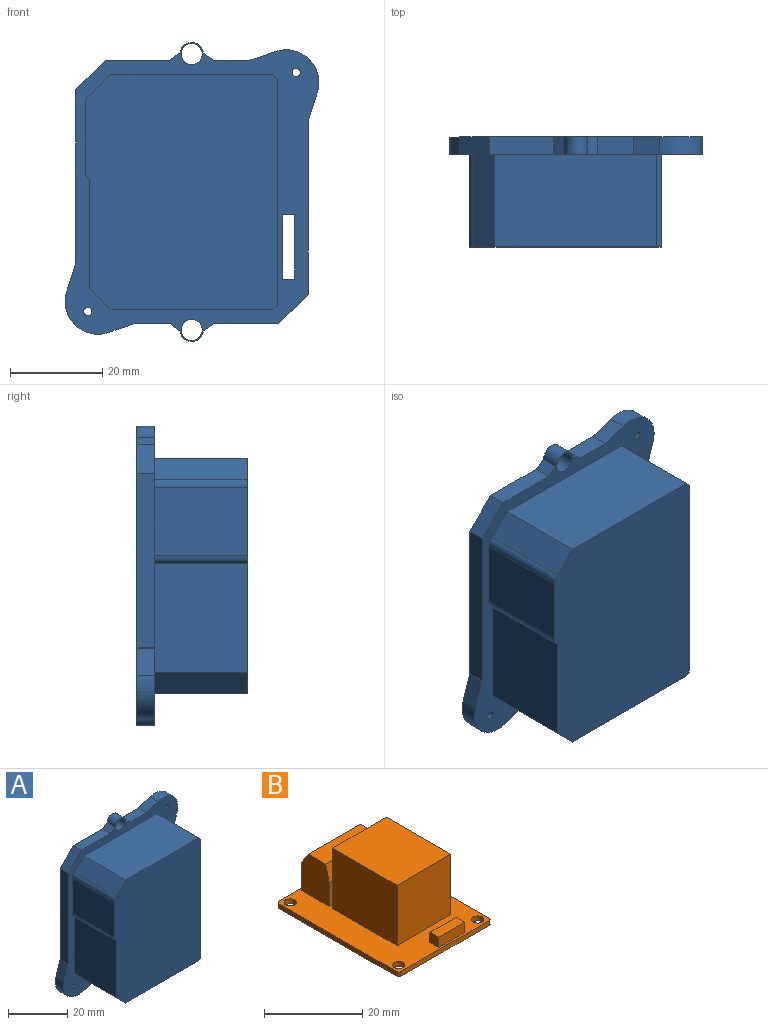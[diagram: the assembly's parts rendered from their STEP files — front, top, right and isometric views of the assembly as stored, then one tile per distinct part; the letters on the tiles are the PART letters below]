
ASSEMBLY  parts=2 mates=1
PART A: 107 faces, bbox 54.9x23.8x64.7 mm
  f0: plane 17x1.5mm, normal (0,0,1), area 25.5mm2, adj f2,f6,f69,f103
  f1: plane 17x1.5mm, normal (0,0,-1), area 25.5mm2, adj f2,f5,f69,f103
  f2: plane 17x14.16mm, normal (1,0,0), area 240.6mm2, adj f0,f1,f69,f103
  f3: plane 3.8x1.5mm, normal (0,0,1), area 5.7mm2, adj f6,f37,f50,f104
  f4: plane 3.8x1.5mm, normal (0,0,-1), area 5.7mm2, adj f5,f37,f50,f104
  f5: plane 22.3x1.39mm, normal (1,0,0), area 28.9mm2, adj f1,f4,f38,f50,f69,f103,f104,f105
  f6: plane 24.98x22.3mm, normal (1,0,0), area 555.1mm2, adj f0,f3,f13,f50,f69,f103,f104,f106
  f7: plane 20.6x6.5mm, normal (1,0,0), area 133.9mm2, adj f8,f43,f67,f70
  f8: plane 6.5x1.9mm, normal (0,0,-1), area 12.3mm2, adj f7,f62,f67,f70
  f9: plane 6.5x1.77mm, normal (0,0,-1), area 11.5mm2, adj f10,f11,f67,f69
  f10: plane 20.28x6.5mm, normal (-1,0,0), area 131.8mm2, adj f9,f13,f67,f69
  f11: plane 25.32x6.5mm, normal (-1,0,0), area 164.6mm2, adj f9,f38,f67,f69
  f12: plane 22.3x21.6mm, normal (-1,0,0), area 475.2mm2, adj f42,f43,f50,f63,f67,f68
  f13: plane 22.3x3.75mm, normal (0.71,0,0.7), area 114.9mm2, adj f6,f10,f43,f50,f67,f69
  f14: plane 3.8x2.6mm, normal (0,0,-1), area 9.9mm2, adj f15,f45,f50,f51
  f15: plane 14.03x3.8mm, normal (-1,0,0), area 53.3mm2, adj f14,f16,f50,f51
  f16: plane 3.8x2.6mm, normal (0,0,1), area 9.9mm2, adj f15,f45,f50,f51
  f17: cylinder r=2.54mm len=5.07mm, axis (0,-1,0), area 28.8mm2, adj f18,f47,f50,f51
  f18: plane 3.8x2.18mm, normal (0.57,0,-0.82), area 10.1mm2, adj f17,f19,f50,f51
  f19: plane 14.1x3.8mm, normal (0,0,-1), area 53.6mm2, adj f18,f20,f50,f51
  f20: plane 6.44x6.43mm, normal (0.71,0,-0.71), area 34.6mm2, adj f19,f21,f50,f51
  f21: plane 37.74x3.8mm, normal (1,0,0), area 143.4mm2, adj f20,f22,f50,f51
  f22: plane 5.76x3.8mm, normal (0.95,0,-0.31), area 23mm2, adj f21,f23,f50,f51
  f23: cylinder r=7.12mm len=9.45mm, axis (0,-1,0), area 60.2mm2, adj f22,f24,f50,f51
  f24: plane 5.46x3.8mm, normal (-0.33,0,0.94), area 21.9mm2, adj f23,f25,f50,f51
  f25: plane 7.84x3.8mm, normal (0,0,1), area 29.8mm2, adj f24,f26,f50,f51
  f26: plane 3.8x2.23mm, normal (0.57,0,0.82), area 10.3mm2, adj f25,f27,f50,f51
  f27: cylinder r=2.54mm len=5.07mm, axis (0,-1,0), area 28.8mm2, adj f26,f28,f50,f51
  f28: plane 3.8x2.2mm, normal (-0.58,0,0.81), area 10.3mm2, adj f27,f29,f50,f51
  f29: plane 13.99x3.8mm, normal (0,0,1), area 53.1mm2, adj f28,f30,f50,f51
  f30: plane 6.36x6.33mm, normal (-0.71,0,0.71), area 34.1mm2, adj f29,f31,f50,f51
  f31: plane 37.62x3.8mm, normal (-1,0,0), area 143mm2, adj f30,f32,f50,f51
  f32: plane 3.8x0.16mm, normal (-0.89,0,0.45), area 0.7mm2, adj f31,f33,f50,f51
  f33: plane 5.76x3.8mm, normal (-0.95,0,0.31), area 23mm2, adj f32,f34,f50,f51
  f34: cylinder r=7.12mm len=9.45mm, axis (0,-1,0), area 60.2mm2, adj f33,f35,f50,f51
  f35: plane 5.37x3.8mm, normal (0.33,0,-0.94), area 21.6mm2, adj f34,f36,f50,f51
  f36: plane 7.88x3.8mm, normal (0,0,-1), area 29.9mm2, adj f35,f47,f50,f51
  f37: plane 14.16x3.8mm, normal (1,0,0), area 53.8mm2, adj f3,f4,f50,f104
  f38: plane 22.3x3.72mm, normal (0.71,0,-0.71), area 104.6mm2, adj f5,f11,f39,f50,f65,f67,f69,f71
  f39: plane 33.71x22.3mm, normal (0,0,-1), area 751.8mm2, adj f38,f40,f50,f71
  f40: plane 22.3x0.58mm, normal (-0.7,0,-0.71), area 18.3mm2, adj f39,f41,f50,f71
  f41: plane 25.83x22.3mm, normal (-1,0,0), area 474.6mm2, adj f40,f42,f50,f71,f74,f75,f76,f77
  f42: plane 22.3x0.5mm, normal (0,0,1), area 11.2mm2, adj f12,f41,f50,f64,f71
  f43: plane 33.78x22.3mm, normal (0,0,1), area 737.8mm2, adj f7,f12,f13,f50,f62,f66,f67,f68
  f44: cylinder r=0.9mm len=3.8mm, axis (0,-1,0), area 21.5mm2, adj f50,f51
  f45: plane 14.03x3.8mm, normal (1,0,0), area 53.3mm2, adj f14,f16,f50,f51
  f46: cylinder r=2.27mm len=4.53mm, axis (0,-1,0), area 54.1mm2, adj f50,f51
  f47: plane 3.8x2.15mm, normal (-0.58,0,-0.81), area 10.1mm2, adj f17,f36,f50,f51
  f48: cylinder r=2.27mm len=4.53mm, axis (0,-1,0), area 54.1mm2, adj f50,f51
  f49: cylinder r=0.9mm len=3.8mm, axis (0,-1,0), area 21.5mm2, adj f50,f51
  f50: plane 64.74x54.9mm, normal (0,1,0), area 1046.7mm2, adj f3,f4,f5,f6,f12,f13,f14,f15
  f51: plane 64.74x54.9mm, normal (0,-1,0), area 806.5mm2, adj f14,f15,f16,f17,f18,f19,f20,f21
  f52: plane 23.6x20mm, normal (-1,0,0), area 472mm2, adj f51,f53,f61,f73
  f53: plane 20x4.64mm, normal (-0.71,0,-0.7), area 130.5mm2, adj f51,f52,f54,f61
  f54: plane 35.03x20mm, normal (0,0,-1), area 700.5mm2, adj f51,f53,f55,f61
  f55: plane 20x0.88mm, normal (0.71,0,-0.71), area 24.9mm2, adj f51,f54,f56,f61
  f56: plane 49.17x20mm, normal (1,0,0), area 882.1mm2, adj f51,f55,f57,f61,f74,f75,f76,f77
  f57: plane 20x0.97mm, normal (0.7,0,0.71), area 27.2mm2, adj f51,f56,f58,f61
  f58: plane 34.95x20mm, normal (0,0,1), area 699mm2, adj f51,f57,f59,f61
  f59: plane 20x4.6mm, normal (-0.71,0,0.71), area 129.8mm2, adj f51,f58,f61,f72
  f60: plane 20x14.7mm, normal (-1,0,0), area 294mm2, adj f51,f61,f72,f73
  f61: plane 51x41.5mm, normal (0,-1,0), area 2060.7mm2, adj f52,f53,f54,f55,f56,f57,f58,f59
  f62: plane 20.6x6.5mm, normal (-1,0,0), area 133.9mm2, adj f8,f43,f67,f70
  f63: plane 29.5x6.5mm, normal (0,0,-1), area 191.7mm2, adj f12,f66,f67,f68
  f64: plane 34.52x6.5mm, normal (0,0,1), area 224.4mm2, adj f42,f65,f67,f71
  f65: plane 25.68x6.5mm, normal (1,0,0), area 166.9mm2, adj f38,f64,f67,f71
  f66: plane 20.6x6.5mm, normal (1,0,0), area 133.9mm2, adj f43,f63,f67,f68
  f67: plane 47.28x35.87mm, normal (0,1,0), area 125.2mm2, adj f7,f8,f9,f10,f11,f12,f13,f38
  f68: plane 29.5x20.6mm, normal (0,1,0), area 607.7mm2, adj f12,f43,f63,f66
  f69: plane 45.6x4.9mm, normal (0,1,0), area 124.3mm2, adj f0,f1,f2,f5,f6,f9,f10,f11
  f70: plane 20.6x1.9mm, normal (0,1,0), area 39.1mm2, adj f7,f8,f43,f62
  f71: plane 35.02x26.4mm, normal (0,1,0), area 924.2mm2, adj f38,f39,f40,f41,f42,f64,f65
  f72: cylinder r=2mm len=20mm, axis (0,1,0), area 41.9mm2, adj f51,f59,f60,f61
  f73: cylinder r=2mm len=20mm, axis (0,1,0), area 41.9mm2, adj f51,f52,f60,f61
  f74: plane 10.97x1mm, normal (0,-1,0), area 11mm2, adj f41,f56,f78,f81
  f75: plane 3x1mm, normal (0,0,-1), area 3mm2, adj f41,f56,f78,f79
  f76: plane 10.97x1mm, normal (0,1,0), area 11mm2, adj f41,f56,f79,f80
  f77: plane 3x1mm, normal (0,0,1), area 3mm2, adj f41,f56,f80,f81
  f78: cylinder r=2mm len=2mm, axis (-1,0,0), area 3.1mm2, adj f41,f56,f74,f75
  f79: cylinder r=2mm len=2mm, axis (-1,0,0), area 3.1mm2, adj f41,f56,f75,f76
  f80: cylinder r=2mm len=2mm, axis (-1,0,0), area 3.1mm2, adj f41,f56,f76,f77
  f81: cylinder r=2mm len=2mm, axis (-1,0,0), area 3.1mm2, adj f41,f56,f74,f77
  f82: plane 14.92x1.5mm, normal (1,0,0), area 22.4mm2, adj f103,f104,f105,f106
  f83: plane 1.5x0.8mm, normal (0,0,-1), area 1.2mm2, adj f84,f98,f103,f104
  f84: plane 1.5x0.8mm, normal (-1,0,0), area 1.2mm2, adj f83,f85,f103,f104
  f85: plane 1.5x0.8mm, normal (0,0,1), area 1.2mm2, adj f84,f98,f103,f104
  f86: plane 1.5x0.8mm, normal (0,0,-1), area 1.2mm2, adj f87,f99,f103,f104
  f87: plane 1.5x0.8mm, normal (-1,0,0), area 1.2mm2, adj f86,f88,f103,f104
  f88: plane 1.5x0.8mm, normal (0,0,1), area 1.2mm2, adj f87,f99,f103,f104
  f89: plane 1.5x0.8mm, normal (0,0,-1), area 1.2mm2, adj f90,f100,f103,f104
  f90: plane 1.5x0.8mm, normal (-1,0,0), area 1.2mm2, adj f89,f91,f103,f104
  f91: plane 1.5x0.8mm, normal (0,0,1), area 1.2mm2, adj f90,f100,f103,f104
  f92: plane 1.5x0.8mm, normal (0,0,-1), area 1.2mm2, adj f93,f101,f103,f104
  f93: plane 1.5x0.8mm, normal (-1,0,0), area 1.2mm2, adj f92,f94,f103,f104
  f94: plane 1.5x0.8mm, normal (0,0,1), area 1.2mm2, adj f93,f101,f103,f104
  f95: plane 1.5x0.8mm, normal (0,0,-1), area 1.2mm2, adj f96,f102,f103,f104
  f96: plane 1.5x0.8mm, normal (-1,0,0), area 1.2mm2, adj f95,f97,f103,f104
  f97: plane 1.5x0.8mm, normal (0,0,1), area 1.2mm2, adj f96,f102,f103,f104
  f98: plane 1.5x0.8mm, normal (1,0,0), area 1.2mm2, adj f83,f85,f103,f104
  f99: plane 1.5x0.8mm, normal (1,0,0), area 1.2mm2, adj f86,f88,f103,f104
  f100: plane 1.5x0.8mm, normal (1,0,0), area 1.2mm2, adj f89,f91,f103,f104
  f101: plane 1.5x0.8mm, normal (1,0,0), area 1.2mm2, adj f92,f94,f103,f104
  f102: plane 1.5x0.8mm, normal (1,0,0), area 1.2mm2, adj f95,f97,f103,f104
  f103: plane 16.92x2.5mm, normal (0,-1,0), area 33.9mm2, adj f0,f1,f2,f5,f6,f82,f83,f84
  f104: plane 16.92x2.5mm, normal (0,1,0), area 33.9mm2, adj f3,f4,f5,f6,f37,f82,f83,f84
  f105: plane 1.5x1mm, normal (0.71,0,0.71), area 2.1mm2, adj f5,f82,f103,f104
  f106: plane 1.5x1mm, normal (0.71,0,-0.71), area 2.1mm2, adj f6,f82,f103,f104
PART B: 31 faces, bbox 26.5x35x16.2 mm
  f0: plane 35x26.5mm, normal (0,0,1), area 481.9mm2, adj f1,f2,f3,f4,f5,f6,f7,f8
  f1: cylinder r=0.5mm len=1.2mm, axis (0,0,1), area 0.9mm2, adj f0,f2,f12,f13
  f2: plane 34x1.2mm, normal (-1,0,0), area 40.8mm2, adj f0,f1,f3,f13
  f3: cylinder r=0.5mm len=1.2mm, axis (0,0,1), area 0.9mm2, adj f0,f2,f4,f13
  f4: plane 25.5x1.2mm, normal (0,-1,0), area 30.6mm2, adj f0,f3,f5,f13
  f5: cylinder r=0.5mm len=1.2mm, axis (0,0,1), area 0.9mm2, adj f0,f4,f6,f13
  f6: plane 34x1.2mm, normal (1,0,0), area 40.8mm2, adj f0,f5,f7,f13
  f7: cylinder r=0.5mm len=1.2mm, axis (0,0,1), area 0.9mm2, adj f0,f6,f12,f13
  f8: cylinder r=1.25mm len=2.5mm, axis (0,0,1), area 9.4mm2, adj f0,f13
  f9: cylinder r=1.25mm len=2.5mm, axis (0,0,1), area 9.4mm2, adj f0,f13
  f10: cylinder r=1.25mm len=2.5mm, axis (0,0,1), area 9.4mm2, adj f0,f13
  f11: cylinder r=1.25mm len=2.5mm, axis (0,0,1), area 9.4mm2, adj f0,f13
  f12: plane 25.5x1.2mm, normal (0,1,0), area 30.6mm2, adj f0,f1,f7,f13
  f13: plane 35x26.5mm, normal (0,0,-1), area 907.7mm2, adj f1,f2,f3,f4,f5,f6,f7,f8
  f14: plane 15x7mm, normal (0,1,0), area 105mm2, adj f0,f15,f17,f19
  f15: plane 10x8mm, normal (-1,0,0), area 75mm2, adj f0,f14,f16,f18,f19,f20
  f16: plane 15x6mm, normal (0,-1,0), area 90mm2, adj f0,f15,f17,f20
  f17: plane 10x8mm, normal (1,0,0), area 75mm2, adj f0,f14,f16,f18,f19,f20
  f18: plane 15x5mm, normal (0,0,1), area 75mm2, adj f15,f17,f19,f20
  f19: plane 15x3mm, normal (0,0.83,0.55), area 54.1mm2, adj f14,f15,f17,f18
  f20: plane 15x4mm, normal (0,-0.97,0.24), area 61.8mm2, adj f15,f16,f17,f18
  f21: plane 15.5x15mm, normal (0,1,0), area 232.5mm2, adj f0,f22,f24,f25
  f22: plane 18.5x15mm, normal (-1,0,0), area 277.5mm2, adj f0,f21,f23,f25
  f23: plane 15.5x15mm, normal (0,-1,0), area 232.5mm2, adj f0,f22,f24,f25
  f24: plane 18.5x15mm, normal (1,0,0), area 277.5mm2, adj f0,f21,f23,f25
  f25: plane 18.5x15.5mm, normal (0,0,1), area 286.8mm2, adj f21,f22,f23,f24
  f26: plane 7.5x2.54mm, normal (0,-1,0), area 19mm2, adj f0,f27,f29,f30
  f27: plane 2.54x2.54mm, normal (1,0,0), area 6.5mm2, adj f0,f26,f28,f30
  f28: plane 7.5x2.54mm, normal (0,1,0), area 19mm2, adj f0,f27,f29,f30
  f29: plane 2.54x2.54mm, normal (-1,0,0), area 6.5mm2, adj f0,f26,f28,f30
  f30: plane 7.5x2.54mm, normal (0,0,1), area 19mm2, adj f26,f27,f28,f29
PLACE A at identity
PLACE B rot(axis=(-0.58,-0.58,-0.58),120deg) t=(-38.65,-17.3,49.79)mm
MATE planar B.f13 <-> A.f71  axis (0,-1,0) through (-21.15,-18.5,36.54)mm
